# Revit family: PRD_AR_WshbsnTps_F5E-MixElectronicWashbasinMixer_F5EM1015 2
name_source: partatom
category: Plumbing Fixtures
units: mm (PartAtom-declared; Revit-internal decimal feet)

## family parameters
Cut with Voids When Loaded = No
Enable Cutting in Views = No
Host = Face
Maintain Annotation Orientation = No
OmniClass Number = 23.45.55.14
OmniClass Title = Single Faucets
Part Type = Normal
Room Calculation Point = No
Round Connector Dimension = Use Diameter
Shared = No

## types (1)
- F5EM1015
    AccentColour = none
    AdjustableFlowTime = yes
    AssetType = Fixed
    BIMObjectName = PRD_AR_WashbasinTaps_F5E-MixElectronicWashbasinMixer_F5EM1015
    BasicColour = chrome-look (glossy)
    Category = Pr_40_20_87_98, Washbasin taps
    CompatibleA3000Open = no
    Default Elevation = 1050 mm
    DefaultAutomaticHygieneFlushing = 24h after the last activity
    Depressurised = no
    Description = F5E-Mix Washbasin mixer DN 15 with angled outlet for installation on fitting units or separate wall flanges, for sanitary facilities. Opto-electronic control, activation on hand reflection. For connection to hot and cold water. Control electronics, solenoid valve cartridge, 6 V lithium battery (CR-P2) and sensor in all-metal housing, high-polished chrome-plated brass. Temperature lever with adjustable, turn-proof temperature stop. Anti-theft aerator, SLIM design, with integrated flow regulator 5.0 l/min. Connections positioned above one another with backflow preventers. Activated water hygiene flushing 24 hours after last activation, safety switch-off for continuous reflexion and saving of statistical data. With option for parameterization and communication via optional, bidirectional remote control.
    DiameterNominal = DN 15
    Export Type to IFC As = IfcValveType
    FaucetFunction = MIXED
    FaucetOperation = TIMEDSELFCLOSING
    FaucetType = SINGLEOUTLETCOMBINATION
    Features = For connection to hot and cold water. High-polished chrome-plated brass. With integrated flow regulator 5.0 l/min.
    Finish = high-polished chromium-plated brass
    FunctionalPrinciple = electronic self-closing
    HygieneFlushing = yes
    IfcExportAs = IfcValveType
    IfcExportType = FAUCET
    Inlet = 15  [stored 0.0492126 ft]
    InletSize = DN 15
    LockingMechanism = Top section, non-ceramic
    Manufacturer = KWC Group Management AG
    ManufacturerName = KWC Group Management AG
    ManufacturerURL = www.kwc-professional.com
    Material = chrome-plated brass
    MaterialFitting = brass-look
    MinimumFlowPressure = 1 bar
    Model = F5EM1015
    ModelNumber = 2030058995
    ModelReference = F5EM1015
    NBSDescription = Water supply fittings for wash basins and troughs
    NBSReference = 45-35-70/371
    Name = F5E-Mix Electronic washbasin mixer for fitting unit or wall flange F5EM1015
    NominalDepth = 195 mm  [stored 0.639764 ft]
    NominalHeight = 0 mm  [stored 0 ft]
    NominalLength = 0 mm  [stored 0 ft]
    NominalWidth = 0 mm  [stored 0 ft]
    NumberOfBatteries = 1
    OutletMaterial = PRD_AR_SyntheticGrey
    Parameterization = remote control
    Pop-UpWasteSet = no
    PowerSupplyConnection = Battery 6 V
    ProductInformation = http://pim.kwc.com
    ProtectiveShutdown = yes
    SensorMaterial = PRD_AR_SyntheticDarkGrey
    SoundInsulation = no
    Spout = fixed
    SpoutProjection = 110 mm
    SurfaceFinishFitting = chromed
    SurfaceTreatmentFitting = polished
    TailorMade = no
    TapMaterial = PRD_AR_ChromatedBrass_HighPolished
    TemperatureLimit = yes
    ThermalDisinfection = automatic thermal disinfection
    Type IFC Predefined Type = FAUCET
    TypeOfBatteries = CR-P2 Lithium battery 6V
    TypeOfMixing = yes
    TypeOfMounting = mounted on product
    TypeOfOperation = sensor operation
    TypeOfPowerSupply = Battery
    TypeOfSensor = opto-electronic sensor
    TypeOfTap = for fitting unit
    URL = www.kwc-professional.com
    Uniclass2015Code = Pr_40_20_87_98
    Uniclass2015Title = Washbasin taps
    Uniclass2015Version = Products v1.38
    Version = 1
    VolumeFlowRateAt3Bar = 0.08 l/s
    WaterConnection = plug connection
    WithBackflowPreventer = yes
    WithFilter = yes
    WithRosettes/CoverPlate = no
    WithTransformer/PowerSupply = no

note: [stored X ft] marks values corroborated as IEEE doubles in the binary element streams (Revit-internal decimal feet)

## geometry (parser evidence)
native form markers: Sweep x5
no freeform markers — native parametric forms only
